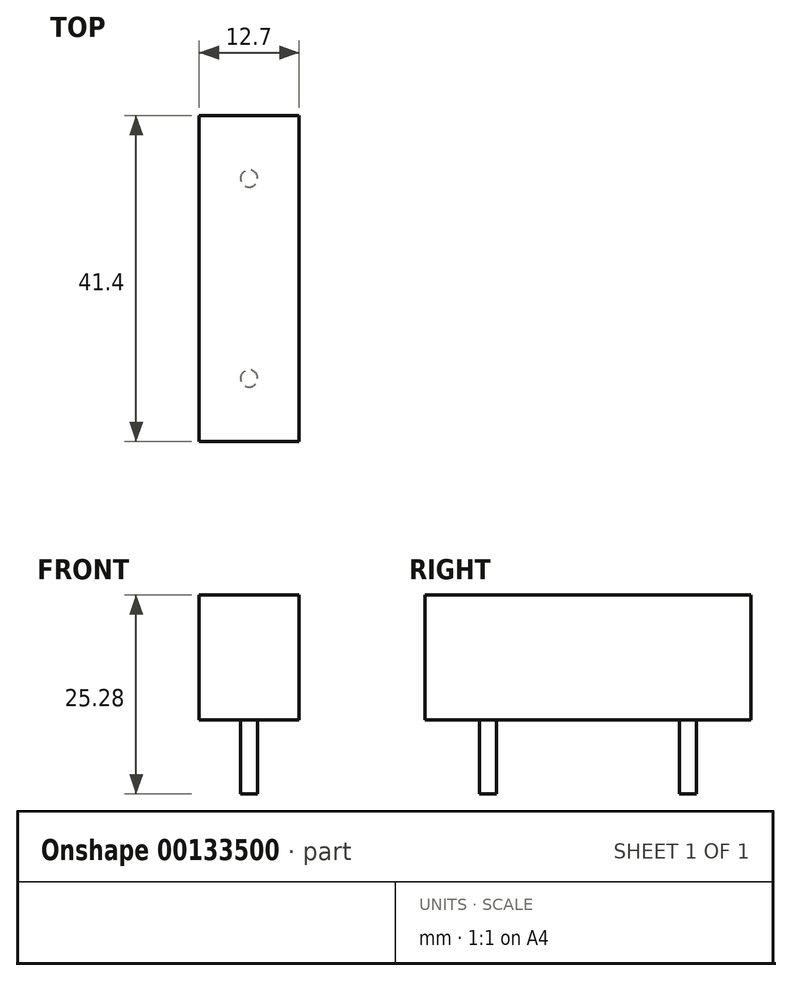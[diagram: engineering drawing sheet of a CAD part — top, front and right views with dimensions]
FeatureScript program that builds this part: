
annotation { "Feature Type Name" : "Feature", "Feature Type Description" : "" }
export const myFeature = defineFeature(function(context is Context, id is Id, definition is map)
    precondition{}
    {
        {
            var Q0;
            Q0=qCreatedBy(makeId("Top.planeOp"),FACE);
            var sketch = newSketch(context, id + "F0", { "sketchPlane" : qUnion([Q0])});
            skLineSegment(sketch, "E0.bottom", {"start": v(6.35, -20.7) * mm, "end": v(-6.35, -20.7) * mm});
            skLineSegment(sketch, "E0.top", {"start": v(6.35, 20.7) * mm, "end": v(-6.35, 20.7) * mm});
            skLineSegment(sketch, "E0.left", {"start": v(6.35, -20.7) * mm, "end": v(6.35, 20.7) * mm});
            skLineSegment(sketch, "E0.right", {"start": v(-6.35, -20.7) * mm, "end": v(-6.35, 20.7) * mm});
            skPoint(sketch, "E0.middle", {"position": v(0, 0) * mm});
            skSolve(sketch);
        }
        {
            var Q0;
            Q0 = qSketchRegion(id + "F0", true);
            extrude(context, id + "F1", {"entities" : qUnion([Q0]), "depth" : 15.88 * mm});
        }
        {
            var Q0;
            Q0=qCreatedBy(makeId("Top.planeOp"),FACE);
            var sketch = newSketch(context, id + "F2", { "sketchPlane" : qUnion([Q0])});
            skLineSegment(sketch, "E1", {"start": v(0, -12.7) * mm, "end": v(0, 12.7) * mm, "construction": true});
            skCircle(sketch, "E2", {"center": v(0, 12.7) * mm, "radius": 1.1 * mm});
            skCircle(sketch, "E3", {"center": v(0, -12.7) * mm, "radius": 1.1 * mm});
            skSolve(sketch);
        }
        {
            var Q0;
            Q0 = qSketchRegion(id + "F2", true);
            extrude(context, id + "F3", {"entities" : qUnion([Q0]), "operationType" : NewBodyOperationType.ADD, "oppositeDirection" : true, "depth" : 9.4 * mm});
        }
    });
